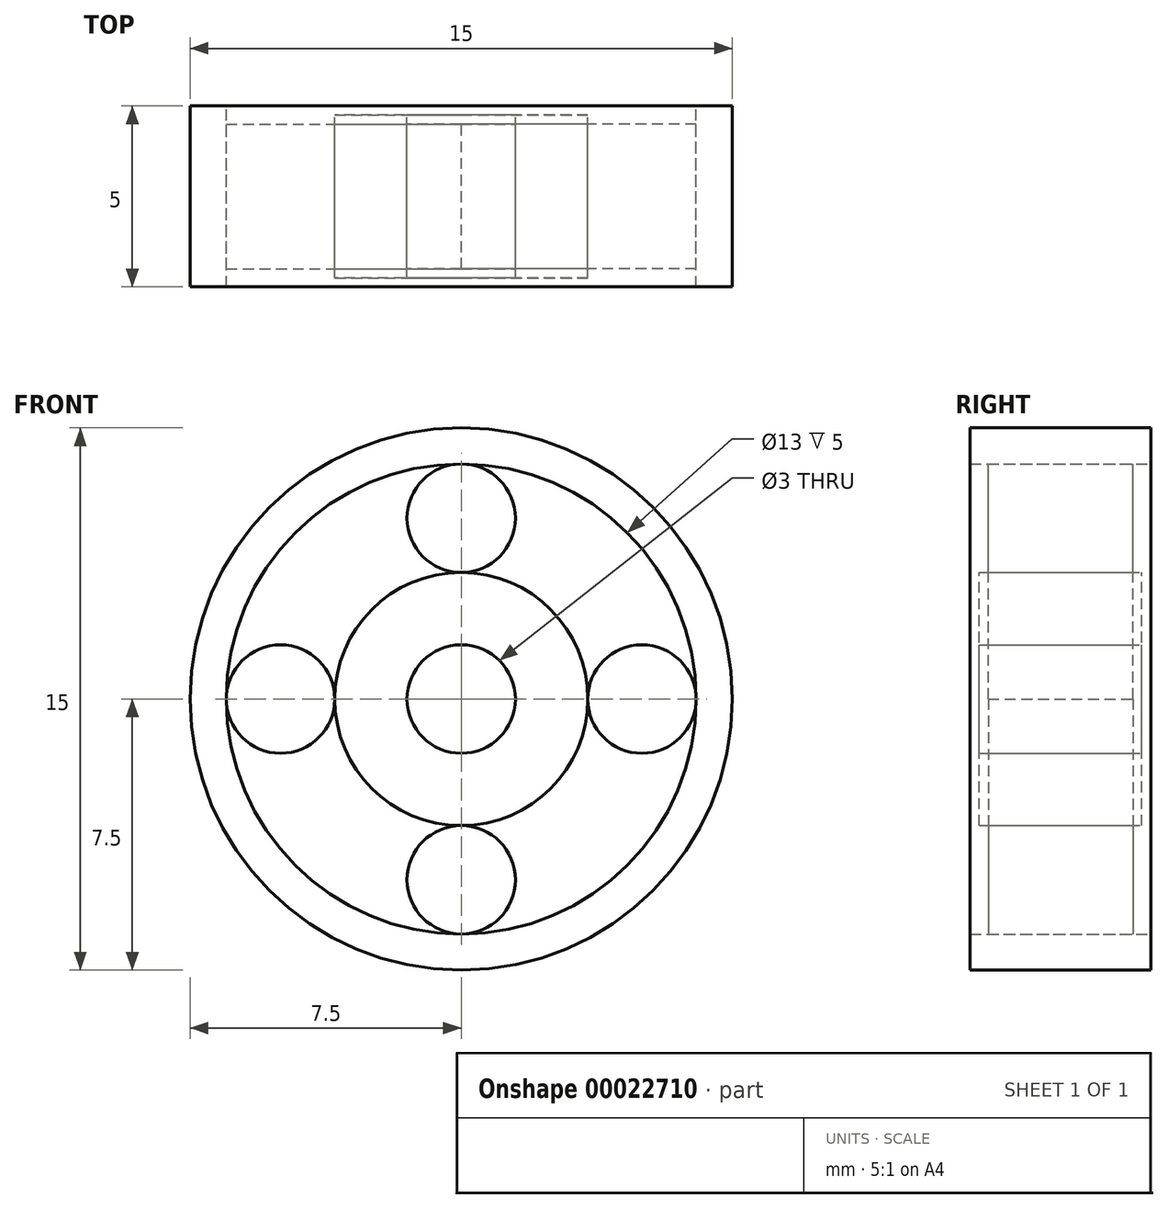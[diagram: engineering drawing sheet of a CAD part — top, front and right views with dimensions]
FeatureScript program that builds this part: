
annotation { "Feature Type Name" : "Feature", "Feature Type Description" : "" }
export const myFeature = defineFeature(function(context is Context, id is Id, definition is map)
    precondition{}
    {
        {
            var Q0;
            Q0=qCreatedBy(makeId("Front.planeOp"),FACE);
            var sketch = newSketch(context, id + "F0", { "sketchPlane" : qUnion([Q0])});
            skCircle(sketch, "E0", {"center": v(0, 0) * mm, "radius": 1.5 * mm});
            skCircle(sketch, "E1", {"center": v(0, 0) * mm, "radius": 3.5 * mm});
            skCircle(sketch, "E2", {"center": v(0, 0) * mm, "radius": 6.5 * mm});
            skCircle(sketch, "E3", {"center": v(0, 0) * mm, "radius": 7.5 * mm});
            skCircle(sketch, "E4", {"center": v(0, 5) * mm, "radius": 1.5 * mm});
            skCircle(sketch, "E5.1.0", {"center": v(-5, 0) * mm, "radius": 1.5 * mm});
            skCircle(sketch, "E5.2.0", {"center": v(0, -5) * mm, "radius": 1.5 * mm});
            skCircle(sketch, "E5.3.0", {"center": v(5, 0) * mm, "radius": 1.5 * mm});
            skSolve(sketch);
        }
        {
            var Q0;
            Q0=makeQuery(id+"F0.imprint","IMPRINT",FACE,{"disambiguationData":[TD([[makeQuery(id+"F0.imprint","IMPRINT",EDGE,{"derivedFrom":sQuery(id+"F0.wireOp",EDGE,"E0")}),-1.0]])]});
            extrude(context, id + "F1", {"entities" : qUnion([Q0]), "endBound" : BoundingType.SYMMETRIC, "depth" : 4.5 * mm});
        }
        {
            var Q0;
            Q0=makeQuery(id+"F0.imprint","IMPRINT",FACE,{"disambiguationData":[TD([[makeQuery(id+"F0.imprint","IMPRINT",EDGE,{"derivedFrom":sQuery(id+"F0.wireOp",EDGE,"E2")}),-1.0]])]});
            extrude(context, id + "F2", {"entities" : qUnion([Q0]), "endBound" : BoundingType.SYMMETRIC, "depth" : 5 * mm});
        }
        {
            var Q0;
            {var subQ3=sQuery(id+"F0.wireOp",EDGE,"E1");var subQ5=sQuery(id+"F0.wireOp",EDGE,"E4");var subQ7=makeQuery(id+"F0.imprint","INTERSECT",VERTEX,{"derivedFrom":[subQ3,subQ5]});Q0=makeQuery(id+"F0.imprint","IMPRINT",FACE,{"disambiguationData":[TD([[makeQuery(id+"F0.imprint","IMPRINT",EDGE,{"disambiguationData":[TD([[subQ7,-1.0]])],"derivedFrom":subQ3}),-1.0]])]});}
            var Q1;
            {var subQ3=sQuery(id+"F0.wireOp",EDGE,"E1");var subQ5=sQuery(id+"F0.wireOp",EDGE,"E4");var subQ7=makeQuery(id+"F0.imprint","INTERSECT",VERTEX,{"derivedFrom":[subQ3,subQ5]});Q1=makeQuery(id+"F0.imprint","IMPRINT",FACE,{"disambiguationData":[TD([[makeQuery(id+"F0.imprint","IMPRINT",EDGE,{"disambiguationData":[TD([[subQ7,1.0]])],"derivedFrom":subQ3}),-1.0]])]});}
            var Q2;
            {var subQ0=sQuery(id+"F0.wireOp",EDGE,"E5.3.0");var subQ3=sQuery(id+"F0.wireOp",EDGE,"E1");var subQ4=makeQuery(id+"F0.imprint","INTERSECT",VERTEX,{"derivedFrom":[subQ3,subQ0]});Q2=makeQuery(id+"F0.imprint","IMPRINT",FACE,{"disambiguationData":[TD([[makeQuery(id+"F0.imprint","IMPRINT",EDGE,{"disambiguationData":[TD([[subQ4,1.0]])],"derivedFrom":subQ3}),-1.0]])]});}
            var Q3;
            {var subQ3=sQuery(id+"F0.wireOp",EDGE,"E1");var subQ5=sQuery(id+"F0.wireOp",EDGE,"E5.1.0");var subQ7=makeQuery(id+"F0.imprint","INTERSECT",VERTEX,{"derivedFrom":[subQ3,subQ5]});Q3=makeQuery(id+"F0.imprint","IMPRINT",FACE,{"disambiguationData":[TD([[makeQuery(id+"F0.imprint","IMPRINT",EDGE,{"disambiguationData":[TD([[subQ7,-1.0]])],"derivedFrom":subQ3}),-1.0]])]});}
            extrude(context, id + "F3", {"entities" : qUnion([Q0, Q1, Q2, Q3]), "endBound" : BoundingType.SYMMETRIC, "depth" : 4 * mm});
        }
    });
